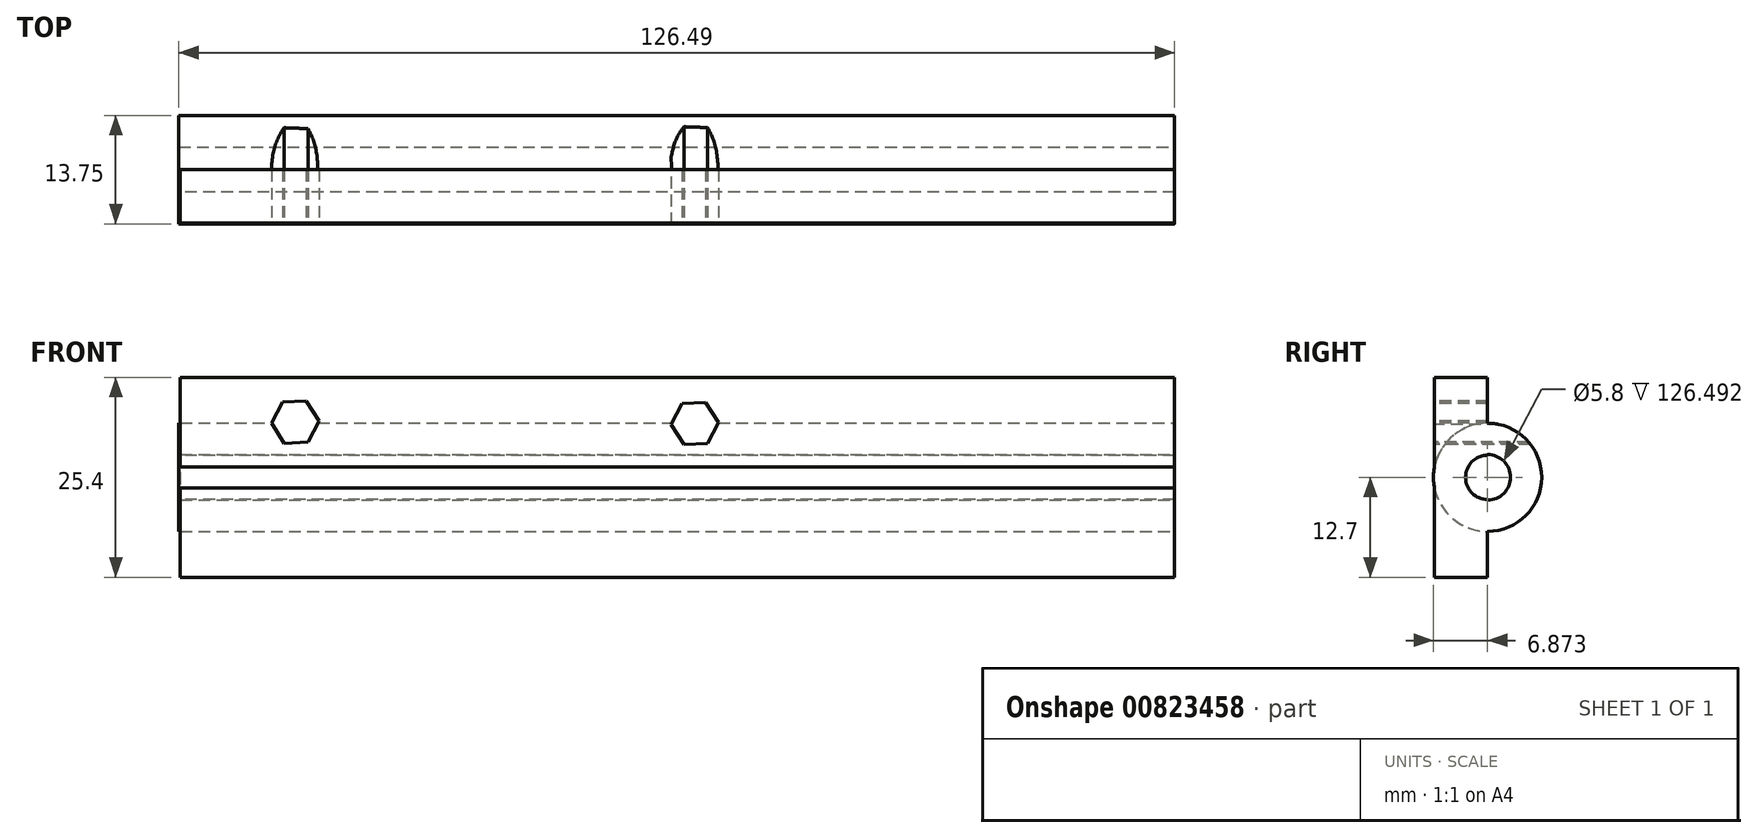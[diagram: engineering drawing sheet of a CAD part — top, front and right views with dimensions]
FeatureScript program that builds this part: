
annotation { "Feature Type Name" : "Feature", "Feature Type Description" : "" }
export const myFeature = defineFeature(function(context is Context, id is Id, definition is map)
    precondition{}
    {
        {
            var Q0;
            Q0=qCreatedBy(makeId("Top.planeOp"),FACE);
            var sketch = newSketch(context, id + "F0", { "sketchPlane" : qUnion([Q0])});
            skLineSegment(sketch, "E0.bottom", {"start": v(63.15, 3.37) * mm, "end": v(-63.15, 3.37) * mm});
            skLineSegment(sketch, "E0.top", {"start": v(63.15, -3.37) * mm, "end": v(-63.15, -3.37) * mm});
            skLineSegment(sketch, "E0.left", {"start": v(63.15, 3.37) * mm, "end": v(63.15, -3.37) * mm});
            skLineSegment(sketch, "E0.right", {"start": v(-63.15, 3.37) * mm, "end": v(-63.15, -3.37) * mm});
            skPoint(sketch, "E0.middle", {"position": v(0, 0) * mm});
            skSolve(sketch);
        }
        {
            var Q0;
            Q0 = qSketchRegion(id + "F0", true);
            extrude(context, id + "F1", {"entities" : qUnion([Q0]), "depth" : 25.4 * mm, "offsetDistance" : 25.4 * mm});
        }
        {
            var Q0;
            Q0=makeQuery(id+"F1.opExtrude","SWEPT_FACE",FACE,{"disambiguationData":[OSD([sQuery(id+"F0.wireOp",EDGE,"E0.left")])]});
            var sketch = newSketch(context, id + "F2", { "sketchPlane" : qUnion([Q0])});
            skArc(sketch, "E1", {"start": v(-3.37, 12.7) * mm, "mid": v(10.1, 12.31) * mm, "end": v(-3.33, 13.48) * mm});
            skSolve(sketch);
        }
        {
            var Q0;
            Q0=sQuery(id+"F2.wireOp",EDGE,"E1");
            extrude(context, id + "F3", {"bodyType" : ToolBodyType.SURFACE, "surfaceEntities" : qUnion([Q0]), "oppositeDirection" : true, "depth" : 125.98 * mm, "offsetDistance" : 25.4 * mm});
        }
        {
            var Q0;
            Q0=makeQuery(id+"F1.opExtrude","SWEPT_FACE",FACE,{"disambiguationData":[OSD([sQuery(id+"F0.wireOp",EDGE,"E0.right")])]});
            var sketch = newSketch(context, id + "F4", { "sketchPlane" : qUnion([Q0])});
            skCircle(sketch, "E2", {"center": v(-3.37, 12.7) * mm, "radius": 2.8 * mm});
            skSolve(sketch);
        }
        {
            var Q0;
            Q0 = qSketchRegion(id + "F4", true);
            extrude(context, id + "F5", {"entities" : qUnion([Q0]), "operationType" : NewBodyOperationType.REMOVE, "oppositeDirection" : true, "depth" : 127 * mm, "offsetDistance" : 25.4 * mm});
        }
        {
            var Q0;
            Q0=makeQuery(id+"F1.opExtrude","SWEPT_FACE",FACE,{"disambiguationData":[OSD([sQuery(id+"F0.wireOp",EDGE,"E0.left")])]});
            var sketch = newSketch(context, id + "F6", { "sketchPlane" : qUnion([Q0])});
            skCircle(sketch, "E3", {"center": v(3.37, 12.7) * mm, "radius": 2.9 * mm});
            skCircle(sketch, "E4", {"center": v(3.37, 12.7) * mm, "radius": 6.87 * mm});
            skSolve(sketch);
        }
        {
            var Q0;
            Q0 = qSketchRegion(id + "F6", true);
            extrude(context, id + "F7", {"entities" : qUnion([Q0]), "operationType" : NewBodyOperationType.ADD, "oppositeDirection" : true, "depth" : 126.5 * mm, "offsetDistance" : 25.4 * mm});
        }
        {
            var Q0;
            {var subQ1=sQuery(id+"F0.wireOp",EDGE,"E0.right");var subQ2=sQuery(id+"F0.wireOp",EDGE,"E0.left");var subQ3=sQuery(id+"F0.wireOp",EDGE,"E0.top");Q0=makeQuery(id+"F7.boolean.opBoolean","SPLIT",FACE,{"disambiguationData":[TD([makeQuery(id+"F1.opExtrude","CAP_FACE",FACE,{"disambiguationData":[OSD([sQuery(id+"F0.wireOp",EDGE,"E0.bottom"),subQ3,subQ2,subQ1])],"isStart":false})])],"derivedFrom":makeQuery(id+"F1.opExtrude","SWEPT_FACE",FACE,{"disambiguationData":[OSD([subQ3])]})});}
            var sketch = newSketch(context, id + "F8", { "sketchPlane" : qUnion([Q0])});
            skCircle(sketch, "E5.cCircle", {"center": v(-48.56, 19.71) * mm, "radius": 2.62 * mm, "construction": true});
            skPoint(sketch, "E5.cCircle.centerSnap0", {"position": v(-63.15, 19.71) * mm});
            skLineSegment(sketch, "E5.0", {"start": v(-47.17, 22.4) * mm, "end": v(-45.54, 19.85) * mm});
            skLineSegment(sketch, "E5.1", {"start": v(-45.54, 19.85) * mm, "end": v(-46.94, 17.17) * mm});
            skLineSegment(sketch, "E5.2", {"start": v(-46.94, 17.17) * mm, "end": v(-49.95, 17.03) * mm});
            skLineSegment(sketch, "E5.3", {"start": v(-49.95, 17.03) * mm, "end": v(-51.58, 19.58) * mm});
            skLineSegment(sketch, "E5.4", {"start": v(-51.58, 19.58) * mm, "end": v(-50.19, 22.26) * mm});
            skLineSegment(sketch, "E5.5", {"start": v(-50.19, 22.26) * mm, "end": v(-47.17, 22.4) * mm});
            skPoint(sketch, "E5.0.midPoint", {"position": v(-46.36, 21.12) * mm});
            skSolve(sketch);
        }
        {
            var Q0;
            Q0=makeQuery(id+"F8.imprint","IMPRINT",FACE,{"disambiguationData":[TD([[makeQuery(id+"F8.imprint","IMPRINT",EDGE,{"derivedFrom":sQuery(id+"F8.wireOp",EDGE,"E5.0")}),-1.0]])]});
            extrude(context, id + "F9", {"entities" : qUnion([Q0]), "operationType" : NewBodyOperationType.REMOVE, "oppositeDirection" : true, "depth" : 12.7 * mm, "offsetDistance" : 25.4 * mm});
        }
        {
            var Q0;
            {var subQ1=sQuery(id+"F0.wireOp",EDGE,"E0.right");var subQ2=sQuery(id+"F0.wireOp",EDGE,"E0.left");var subQ3=sQuery(id+"F0.wireOp",EDGE,"E0.top");Q0=makeQuery(id+"F7.boolean.opBoolean","SPLIT",FACE,{"disambiguationData":[TD([makeQuery(id+"F1.opExtrude","CAP_FACE",FACE,{"disambiguationData":[OSD([sQuery(id+"F0.wireOp",EDGE,"E0.bottom"),subQ3,subQ2,subQ1])],"isStart":false})])],"derivedFrom":makeQuery(id+"F1.opExtrude","SWEPT_FACE",FACE,{"disambiguationData":[OSD([subQ3])]})});}
            var sketch = newSketch(context, id + "F10", { "sketchPlane" : qUnion([Q0])});
            skCircle(sketch, "E6.cCircle", {"center": v(2.2, 19.56) * mm, "radius": 2.62 * mm, "construction": true});
            skPoint(sketch, "E6.cCircle.centerSnap0", {"position": v(-12.4, 19.56) * mm});
            skLineSegment(sketch, "E6.0", {"start": v(3.58, 22.24) * mm, "end": v(5.2, 19.7) * mm});
            skLineSegment(sketch, "E6.1", {"start": v(5.2, 19.7) * mm, "end": v(3.82, 17.01) * mm});
            skLineSegment(sketch, "E6.2", {"start": v(3.82, 17.01) * mm, "end": v(0.8, 16.88) * mm});
            skLineSegment(sketch, "E6.3", {"start": v(0.8, 16.88) * mm, "end": v(-0.83, 19.42) * mm});
            skLineSegment(sketch, "E6.4", {"start": v(-0.83, 19.42) * mm, "end": v(0.56, 22.1) * mm});
            skLineSegment(sketch, "E6.5", {"start": v(0.56, 22.1) * mm, "end": v(3.58, 22.24) * mm});
            skPoint(sketch, "E6.0.midPoint", {"position": v(4.4, 20.97) * mm});
            skSolve(sketch);
        }
        {
            var Q0;
            Q0=makeQuery(id+"F10.imprint","IMPRINT",FACE,{"disambiguationData":[TD([[makeQuery(id+"F10.imprint","IMPRINT",EDGE,{"derivedFrom":sQuery(id+"F10.wireOp",EDGE,"E6.0")}),-1.0]])]});
            extrude(context, id + "F11", {"entities" : qUnion([Q0]), "operationType" : NewBodyOperationType.REMOVE, "oppositeDirection" : true, "depth" : 12.7 * mm, "offsetDistance" : 25.4 * mm});
        }
    });
